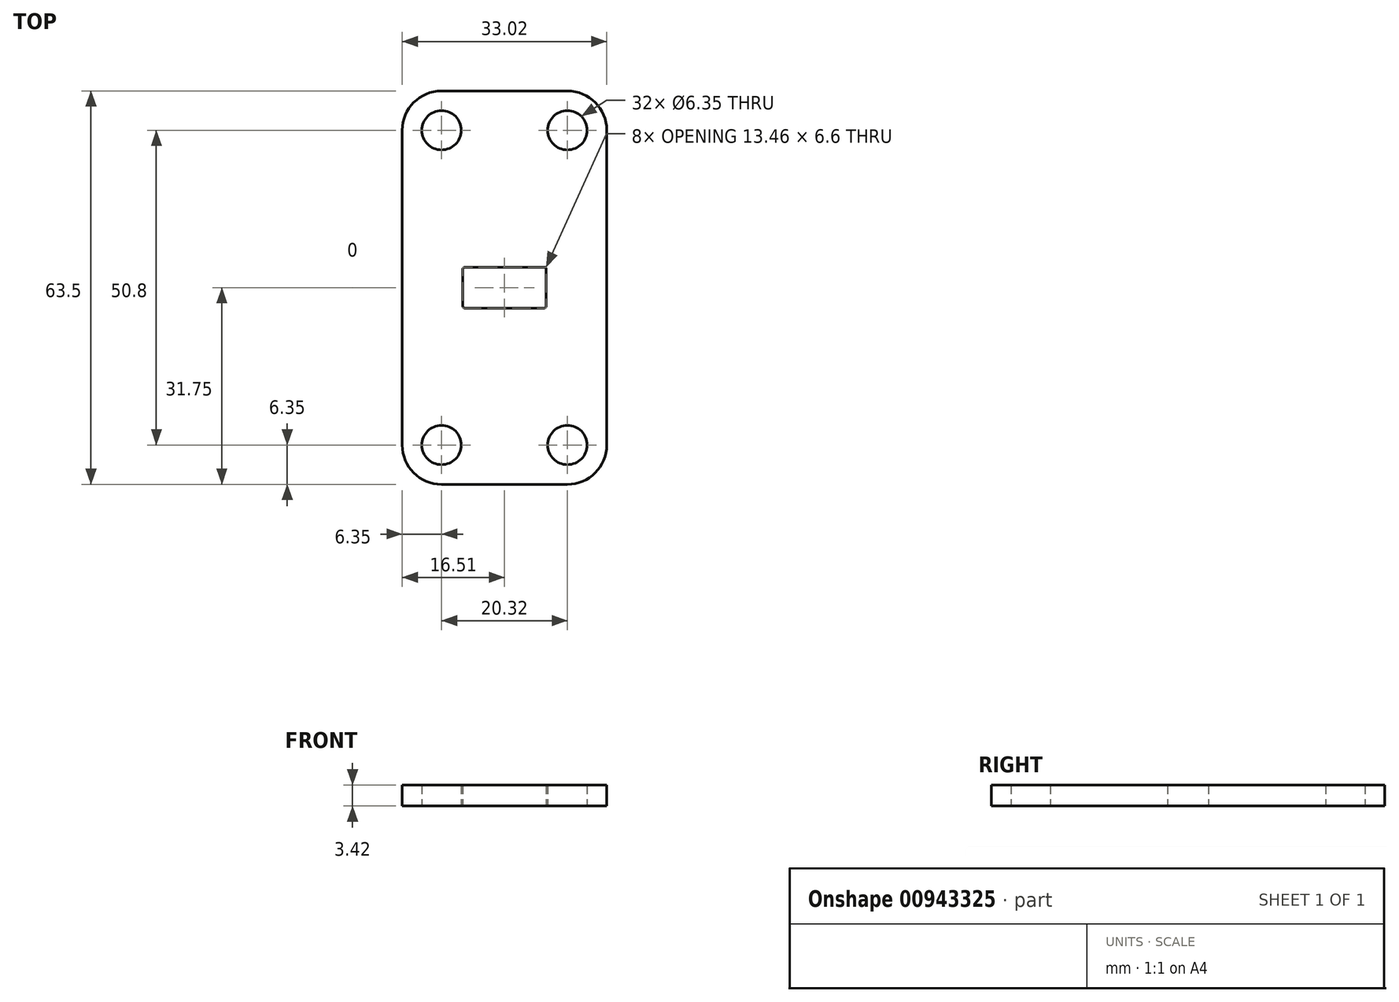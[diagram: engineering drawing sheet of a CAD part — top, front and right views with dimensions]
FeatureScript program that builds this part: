
annotation { "Feature Type Name" : "Feature", "Feature Type Description" : "" }
export const myFeature = defineFeature(function(context is Context, id is Id, definition is map)
    precondition{}
    {
        {
            var Q0;
            Q0=qCreatedBy(makeId("Top.planeOp"),FACE);
            var sketch = newSketch(context, id + "F0", { "sketchPlane" : qUnion([Q0])});
            skLineSegment(sketch, "E0.bottom", {"start": v(10.16, 31.75) * mm, "end": v(-10.16, 31.75) * mm});
            skLineSegment(sketch, "E0.top", {"start": v(10.16, -31.75) * mm, "end": v(-10.16, -31.75) * mm});
            skLineSegment(sketch, "E0.left", {"start": v(16.51, 25.4) * mm, "end": v(16.51, -25.4) * mm});
            skLineSegment(sketch, "E0.right", {"start": v(-16.51, 25.4) * mm, "end": v(-16.51, -25.4) * mm});
            skPoint(sketch, "E0.middle", {"position": v(0, 0) * mm});
            skLineSegment(sketch, "E1.bottom", {"start": v(6.41, 3.3) * mm, "end": v(-6.41, 3.3) * mm});
            skLineSegment(sketch, "E1.top", {"start": v(6.41, -3.3) * mm, "end": v(-6.41, -3.3) * mm});
            skLineSegment(sketch, "E1.left", {"start": v(6.73, 2.98) * mm, "end": v(6.73, -2.98) * mm});
            skLineSegment(sketch, "E1.right", {"start": v(-6.73, 2.98) * mm, "end": v(-6.73, -2.98) * mm});
            skPoint(sketch, "E2.visualSharp", {"position": v(-16.51, 31.75) * mm});
            skArc(sketch, "E2.filletArc", {"start": v(-10.16, 31.75) * mm, "mid": v(-14.65, 29.9) * mm, "end": v(-16.51, 25.4) * mm});
            skPoint(sketch, "E3.visualSharp", {"position": v(-16.51, -31.75) * mm});
            skArc(sketch, "E3.filletArc", {"start": v(-16.51, -25.4) * mm, "mid": v(-14.65, -29.9) * mm, "end": v(-10.16, -31.75) * mm});
            skPoint(sketch, "E4.visualSharp", {"position": v(16.51, -31.75) * mm});
            skArc(sketch, "E4.filletArc", {"start": v(10.16, -31.75) * mm, "mid": v(14.65, -29.9) * mm, "end": v(16.51, -25.4) * mm});
            skPoint(sketch, "E5.visualSharp", {"position": v(16.51, 31.75) * mm});
            skArc(sketch, "E5.filletArc", {"start": v(16.51, 25.4) * mm, "mid": v(14.65, 29.9) * mm, "end": v(10.16, 31.75) * mm});
            skPoint(sketch, "E6.visualSharp", {"position": v(-6.73, 3.3) * mm});
            skArc(sketch, "E6.filletArc", {"start": v(-6.41, 3.3) * mm, "mid": v(-6.64, 3.2) * mm, "end": v(-6.73, 2.98) * mm});
            skPoint(sketch, "E7.visualSharp", {"position": v(-6.73, -3.3) * mm});
            skArc(sketch, "E7.filletArc", {"start": v(-6.73, -2.98) * mm, "mid": v(-6.64, -3.2) * mm, "end": v(-6.41, -3.3) * mm});
            skPoint(sketch, "E8.visualSharp", {"position": v(6.73, -3.3) * mm});
            skArc(sketch, "E8.filletArc", {"start": v(6.41, -3.3) * mm, "mid": v(6.64, -3.2) * mm, "end": v(6.73, -2.98) * mm});
            skPoint(sketch, "E9.visualSharp", {"position": v(6.73, 3.3) * mm});
            skArc(sketch, "E9.filletArc", {"start": v(6.73, 2.98) * mm, "mid": v(6.64, 3.2) * mm, "end": v(6.41, 3.3) * mm});
            skCircle(sketch, "E10", {"center": v(-10.16, 25.4) * mm, "radius": 3.18 * mm});
            skCircle(sketch, "E11", {"center": v(-10.16, -25.4) * mm, "radius": 3.18 * mm});
            skCircle(sketch, "E12", {"center": v(10.16, -25.4) * mm, "radius": 3.18 * mm});
            skCircle(sketch, "E13", {"center": v(10.16, 25.4) * mm, "radius": 3.18 * mm});
            skSolve(sketch);
        }
        {
            var Q0;
            Q0=makeQuery(id+"F0.imprint","IMPRINT",FACE,{"disambiguationData":[TD([[makeQuery(id+"F0.imprint","IMPRINT",EDGE,{"derivedFrom":sQuery(id+"F0.wireOp",EDGE,"E0.bottom")}),1.0]])]});
            extrude(context, id + "F1", {"entities" : qUnion([Q0]), "endBound" : BoundingType.SYMMETRIC, "depth" : 3.42 * mm, "offsetDistance" : 25.4 * mm});
        }
    });
